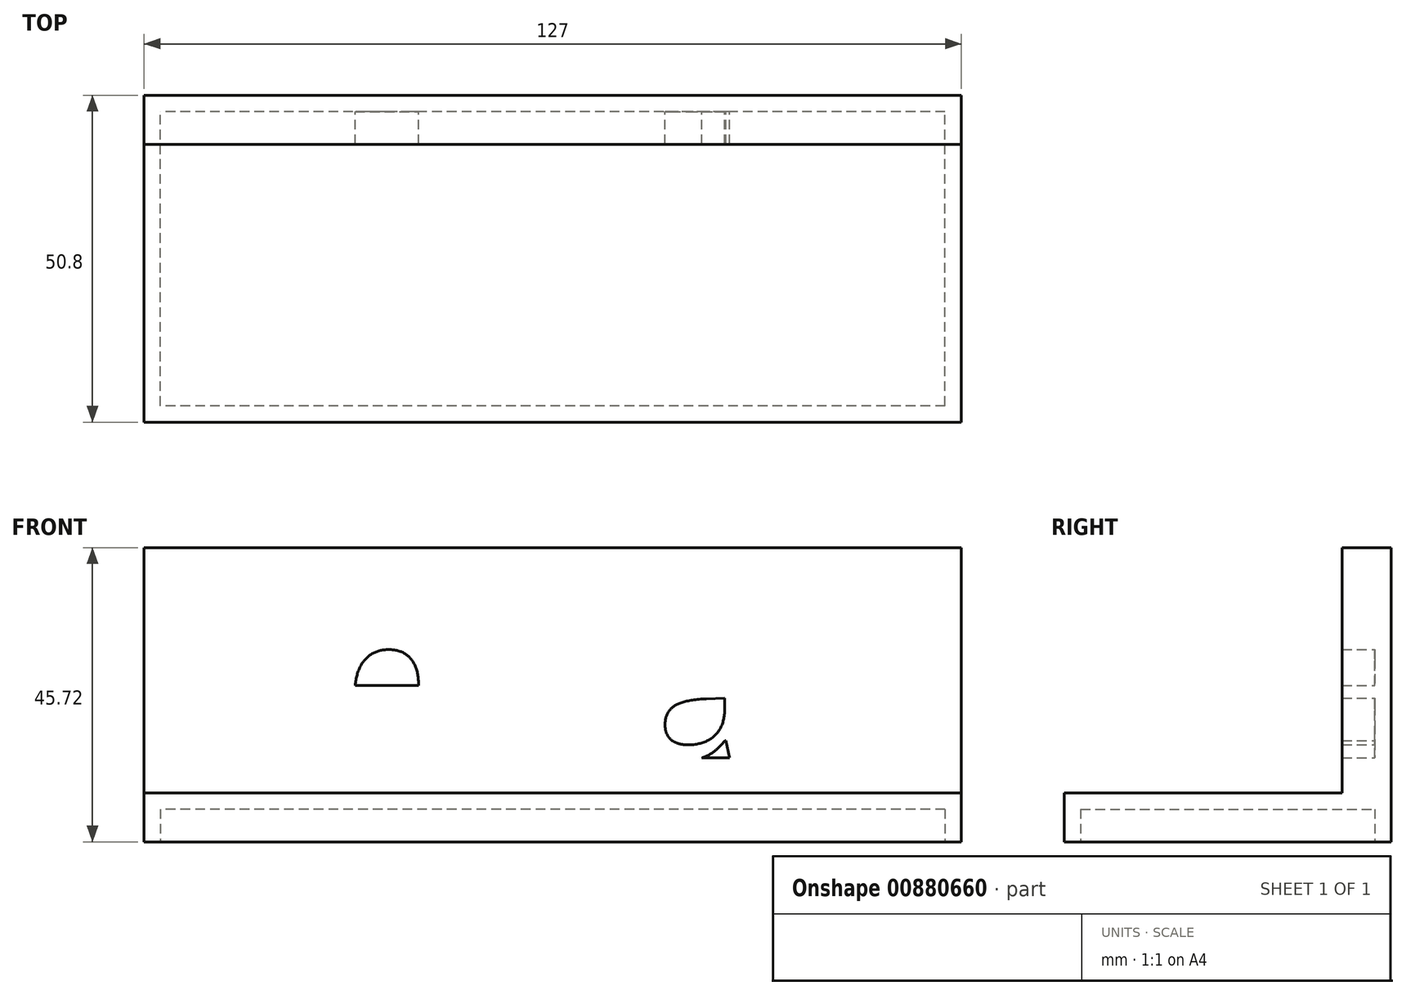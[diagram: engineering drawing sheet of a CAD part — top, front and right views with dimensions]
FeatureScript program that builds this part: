
annotation { "Feature Type Name" : "Feature", "Feature Type Description" : "" }
export const myFeature = defineFeature(function(context is Context, id is Id, definition is map)
    precondition{}
    {
        {
            var Q0;
            Q0=qCreatedBy(makeId("Top.planeOp"),FACE);
            var sketch = newSketch(context, id + "F0", { "sketchPlane" : qUnion([Q0])});
            skLineSegment(sketch, "E0.bottom", {"start": v(63.5, -25.4) * mm, "end": v(-63.5, -25.4) * mm});
            skLineSegment(sketch, "E0.top", {"start": v(63.5, 25.4) * mm, "end": v(-63.5, 25.4) * mm});
            skLineSegment(sketch, "E0.left", {"start": v(63.5, -25.4) * mm, "end": v(63.5, 25.4) * mm});
            skLineSegment(sketch, "E0.right", {"start": v(-63.5, -25.4) * mm, "end": v(-63.5, 25.4) * mm});
            skPoint(sketch, "E0.middle", {"position": v(0, 0) * mm});
            skSolve(sketch);
        }
        {
            var Q0;
            Q0 = qSketchRegion(id + "F0", true);
            extrude(context, id + "F1", {"entities" : qUnion([Q0]), "depth" : 7.62 * mm, "offsetDistance" : 25.4 * mm});
        }
        {
            var Q0;
            Q0=makeQuery(id+"F1.opExtrude","CAP_FACE",FACE,{"disambiguationData":[OSD([sQuery(id+"F0.wireOp",EDGE,"E0.bottom"),sQuery(id+"F0.wireOp",EDGE,"E0.top"),sQuery(id+"F0.wireOp",EDGE,"E0.left"),sQuery(id+"F0.wireOp",EDGE,"E0.right")])],"isStart":true});
            shell(context, id + "F2", {"entities" : qUnion([Q0]), "thickness" : 2.54 * mm});
        }
        {
            var Q0;
            Q0=makeQuery(id+"F1.opExtrude","CAP_FACE",FACE,{"disambiguationData":[OSD([sQuery(id+"F0.wireOp",EDGE,"E0.bottom"),sQuery(id+"F0.wireOp",EDGE,"E0.top"),sQuery(id+"F0.wireOp",EDGE,"E0.left"),sQuery(id+"F0.wireOp",EDGE,"E0.right")])],"isStart":false});
            var sketch = newSketch(context, id + "F3", { "sketchPlane" : qUnion([Q0])});
            skLineSegment(sketch, "E1", {"start": v(-63.5, 25.4) * mm, "end": v(-63.5, 17.78) * mm});
            skLineSegment(sketch, "E2", {"start": v(-63.5, 17.78) * mm, "end": v(63.5, 17.78) * mm});
            skLineSegment(sketch, "E3", {"start": v(63.5, 17.78) * mm, "end": v(63.5, 25.4) * mm});
            skLineSegment(sketch, "E4", {"start": v(63.5, 25.4) * mm, "end": v(-63.5, 25.4) * mm});
            skSolve(sketch);
        }
        {
            var Q0;
            Q0=makeQuery(id+"F3.imprint","IMPRINT",FACE,{"disambiguationData":[TD([[makeQuery(id+"F3.imprint","IMPRINT",EDGE,{"derivedFrom":sQuery(id+"F3.wireOp",EDGE,"E1")}),-1.0]])]});
            extrude(context, id + "F4", {"entities" : qUnion([Q0]), "operationType" : NewBodyOperationType.ADD, "depth" : 38.1 * mm, "offsetDistance" : 25.4 * mm});
        }
        {
            var Q0;
            Q0=makeQuery(id+"F4.opExtrude","SWEPT_FACE",FACE,{"disambiguationData":[OSD([sQuery(id+"F3.wireOp",EDGE,"E2")])]});
            shell(context, id + "F5", {"entities" : qUnion([Q0]), "thickness" : 2.54 * mm});
        }
        {
            var Q0;
            Q0=makeQuery(id+"F5.opShell","OFFSET_FACE",FACE,{"disambiguationData":[OSD([sQuery(id+"F0.wireOp",EDGE,"E0.top"),sQuery(id+"F3.wireOp",EDGE,"E4")])]});
            var sketch = newSketch(context, id + "F6", { "sketchPlane" : qUnion([Q0])});
            skText(sketch, "E5", { "text": "Ferrari", "fontName": "OpenSans-Regular.ttf"});
            const initialGuessF6  = {"E5": [-0.05389, 0.01306, 1, 0, 0.02537]};
            skSetInitialGuess(sketch, initialGuessF6);
            skSolve(sketch);
        }
        {
            var Q0;
            Q0 = qSketchRegion(id + "F6", true);
            extrude(context, id + "F7", {"entities" : qUnion([Q0]), "operationType" : NewBodyOperationType.ADD, "depth" : 5.08 * mm, "offsetDistance" : 25.4 * mm});
        }
        {
            var Q0;
            {var subQ0=sQuery(id+"F3.wireOp",EDGE,"E4");var subQ5=sQuery(id+"F0.wireOp",EDGE,"E0.top");Q0=makeQuery(id+"F7.boolean.opBoolean","SPLIT",FACE,{"disambiguationData":[TD([makeQuery(id+"F7.opExtrude","SWEPT_FACE",FACE,{"disambiguationData":[OSD([sQuery(id+"F6.wireOp",EDGE,"E5.sketch_text.stroke-0")])]})])],"derivedFrom":makeQuery(id+"F5.opShell","OFFSET_FACE",FACE,{"disambiguationData":[OSD([subQ5,subQ0])]})});}
            var sketch = newSketch(context, id + "F8", { "sketchPlane" : qUnion([Q0])});
            skLineSegment(sketch, "E6", {"start": v(-50.43, 13.06) * mm, "end": v(-60.96, 13.06) * mm});
            skLineSegment(sketch, "E7", {"start": v(-50.43, 13.06) * mm, "end": v(60.96, 13.06) * mm});
            skLineSegment(sketch, "E8", {"start": v(60.96, 13.06) * mm, "end": v(60.96, 7.62) * mm});
            skLineSegment(sketch, "E9", {"start": v(60.96, 7.62) * mm, "end": v(-60.96, 7.62) * mm});
            skLineSegment(sketch, "E10", {"start": v(-60.96, 7.62) * mm, "end": v(-60.96, 13.06) * mm});
            skSolve(sketch);
        }
        {
            var Q0;
            Q0 = qSketchRegion(id + "F8", true);
            extrude(context, id + "F9", {"entities" : qUnion([Q0]), "operationType" : NewBodyOperationType.ADD, "depth" : 5.08 * mm, "offsetDistance" : 25.4 * mm});
        }
        {
            var Q0;
            {var subQ35=sQuery(id+"F3.wireOp",EDGE,"E4");var subQ52=makeQuery(id+"F7.opExtrude","SWEPT_FACE",FACE,{"disambiguationData":[OSD([sQuery(id+"F6.wireOp",EDGE,"E5.sketch_text.stroke-1")])]});var subQ91=sQuery(id+"F0.wireOp",EDGE,"E0.top");Q0=makeQuery(id+"F9.boolean.opBoolean","SPLIT",FACE,{"disambiguationData":[TD([subQ52])],"derivedFrom":makeQuery(id+"F7.boolean.opBoolean","SPLIT",FACE,{"disambiguationData":[TD([makeQuery(id+"F7.opExtrude","SWEPT_FACE",FACE,{"disambiguationData":[OSD([sQuery(id+"F6.wireOp",EDGE,"E5.sketch_text.stroke-0")])]})])],"derivedFrom":makeQuery(id+"F5.opShell","OFFSET_FACE",FACE,{"disambiguationData":[OSD([subQ91,subQ35])]})})});}
            var sketch = newSketch(context, id + "F10", { "sketchPlane" : qUnion([Q0])});
            skLineSegment(sketch, "E11", {"start": v(-36.4, 38.21) * mm, "end": v(52.47, 38.45) * mm});
            skLineSegment(sketch, "E12", {"start": v(52.47, 38.45) * mm, "end": v(52.47, 35.59) * mm});
            skLineSegment(sketch, "E13", {"start": v(52.47, 35.59) * mm, "end": v(-36.4, 35.62) * mm});
            skSolve(sketch);
        }
        {
            var Q0;
            {var subQ5=makeQuery(id+"F7.opExtrude","CAP_EDGE",EDGE,{"disambiguationData":[OSD([sQuery(id+"F6.wireOp",EDGE,"E5.sketch_text.stroke-3")])],"isStart":true});Q0=makeQuery(id+"F10.imprint","IMPRINT",FACE,{"disambiguationData":[TD([[makeQuery(id+"F10.imprint","IMPRINT",EDGE,{"derivedFrom":subQ5}),1.0]])]});}
            extrude(context, id + "F11", {"entities" : qUnion([Q0]), "operationType" : NewBodyOperationType.ADD, "depth" : 5.08 * mm, "offsetDistance" : 25.4 * mm});
        }
    });
